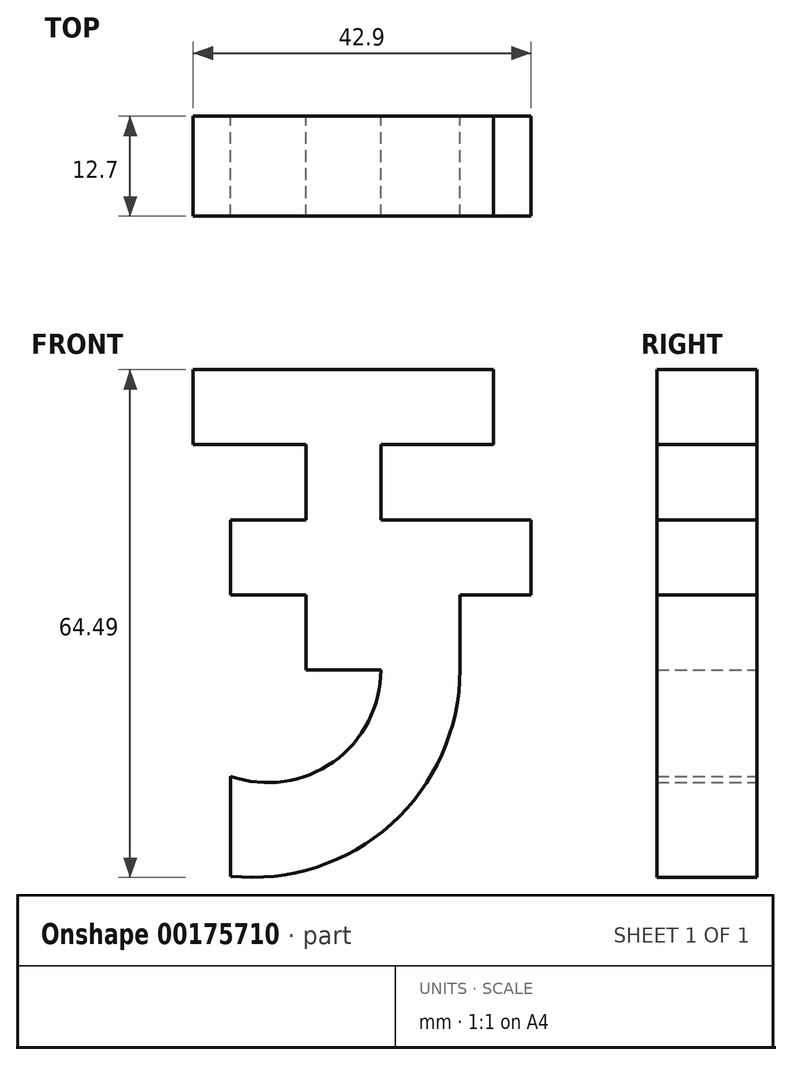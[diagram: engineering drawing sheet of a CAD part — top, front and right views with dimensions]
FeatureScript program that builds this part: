
annotation { "Feature Type Name" : "Feature", "Feature Type Description" : "" }
export const myFeature = defineFeature(function(context is Context, id is Id, definition is map)
    precondition{}
    {
        {
            var Q0;
            Q0=qCreatedBy(makeId("Front.planeOp"),FACE);
            var sketch = newSketch(context, id + "F0", { "sketchPlane" : qUnion([Q0])});
            skLineSegment(sketch, "E0.bottom", {"start": v(0, 0) * mm, "end": v(9.53, 0) * mm});
            skLineSegment(sketch, "E0.top", {"start": v(0, 38.14) * mm, "end": v(9.53, 38.14) * mm});
            skLineSegment(sketch, "E0.left", {"start": v(0, 0) * mm, "end": v(0, 9.53) * mm});
            skLineSegment(sketch, "E1.bottom", {"start": v(0, 38.14) * mm, "end": v(-14.3, 38.14) * mm});
            skLineSegment(sketch, "E1.top", {"start": v(0, 28.6) * mm, "end": v(-14.3, 28.6) * mm});
            skLineSegment(sketch, "E1.right", {"start": v(-14.3, 38.14) * mm, "end": v(-14.3, 28.6) * mm});
            skLineSegment(sketch, "E2.bottom", {"start": v(9.53, 38.14) * mm, "end": v(23.83, 38.14) * mm});
            skLineSegment(sketch, "E2.top", {"start": v(9.53, 28.6) * mm, "end": v(23.83, 28.6) * mm});
            skLineSegment(sketch, "E2.right", {"start": v(23.83, 38.14) * mm, "end": v(23.83, 28.6) * mm});
            skPoint(sketch, "E3", {"position": v(0, 19.07) * mm});
            skLineSegment(sketch, "E4.bottom", {"start": v(0, 19.07) * mm, "end": v(-9.53, 19.07) * mm});
            skLineSegment(sketch, "E4.top", {"start": v(0, 9.53) * mm, "end": v(-9.53, 9.53) * mm});
            skLineSegment(sketch, "E4.right", {"start": v(-9.53, 19.07) * mm, "end": v(-9.53, 9.53) * mm});
            skLineSegment(sketch, "E5.bottom", {"start": v(9.53, 19.07) * mm, "end": v(28.6, 19.07) * mm});
            skLineSegment(sketch, "E5.top", {"start": v(19.57, 9.53) * mm, "end": v(28.6, 9.53) * mm});
            skLineSegment(sketch, "E5.right", {"start": v(28.6, 19.07) * mm, "end": v(28.6, 9.53) * mm});
            skLineSegment(sketch, "E6.right", {"start": v(19.57, 9.53) * mm, "end": v(19.57, 0) * mm});
            skPoint(sketch, "E7.start.orphan", {"position": v(0, -10.97) * mm});
            skPoint(sketch, "E8.start.orphan", {"position": v(0, -20.5) * mm});
            skLineSegment(sketch, "E9", {"start": v(-9.53, -13.5) * mm, "end": v(-9.53, -26.2) * mm});
            skArc(sketch, "E10", {"start": v(-9.53, -13.5) * mm, "mid": v(3.5, -11.68) * mm, "end": v(9.53, 0) * mm});
            skArc(sketch, "E11", {"start": v(-9.53, -26.2) * mm, "mid": v(10.85, -19.58) * mm, "end": v(19.57, 0) * mm});
            skPoint(sketch, "E12.orphan", {"position": v(-9.53, -36.55) * mm});
            skLineSegment(sketch, "E13.trimOffspring", {"start": v(0, 19.07) * mm, "end": v(0, 28.6) * mm});
            skLineSegment(sketch, "E14.trimOffspring", {"start": v(9.53, 19.07) * mm, "end": v(9.53, 28.6) * mm});
            skSolve(sketch);
        }
        {
            var Q0;
            Q0 = qSketchRegion(id + "F0", true);
            extrude(context, id + "F1", {"entities" : qUnion([Q0]), "depth" : 12.7 * mm});
        }
    });
